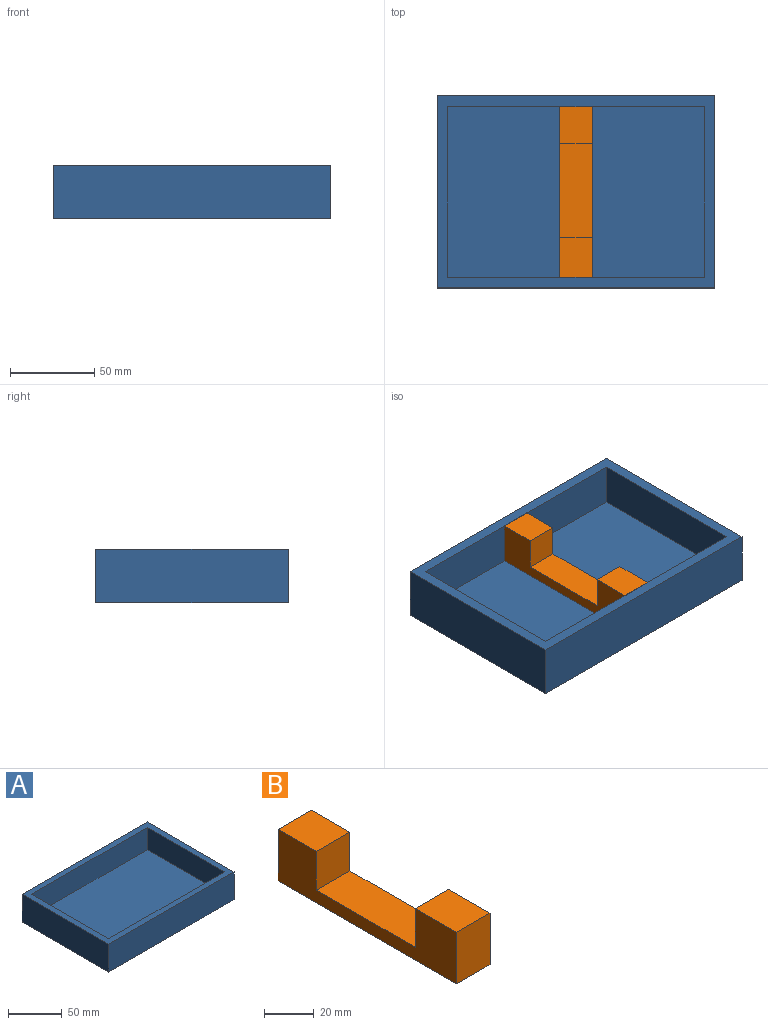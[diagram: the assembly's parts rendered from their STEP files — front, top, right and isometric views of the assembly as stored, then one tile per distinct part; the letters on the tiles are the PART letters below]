
ASSEMBLY  parts=2 mates=1
PART A: 11 faces, bbox 165.1x114.3x31.8 mm
  f0: plane 165.1x114.3mm, normal (0,0,1), area 3387.1mm2, adj f1,f2,f3,f4,f6,f7,f8,f9
  f1: plane 114.3x31.75mm, normal (1,0,0), area 3629mm2, adj f0,f2,f4,f5
  f2: plane 165.1x31.75mm, normal (0,1,0), area 5241.9mm2, adj f0,f1,f3,f5
  f3: plane 114.3x31.75mm, normal (-1,0,0), area 3629mm2, adj f0,f2,f4,f5
  f4: plane 165.1x31.75mm, normal (0,-1,0), area 5241.9mm2, adj f0,f1,f3,f5
  f5: plane 165.1x114.3mm, normal (0,0,-1), area 18870.9mm2, adj f1,f2,f3,f4
  f6: plane 101.6x25.4mm, normal (-1,0,0), area 2580.6mm2, adj f0,f7,f9,f10
  f7: plane 152.4x25.4mm, normal (0,-1,0), area 3871mm2, adj f0,f6,f8,f10
  f8: plane 101.6x25.4mm, normal (1,0,0), area 2580.6mm2, adj f0,f7,f9,f10
  f9: plane 152.4x25.4mm, normal (0,1,0), area 3871mm2, adj f0,f6,f8,f10
  f10: plane 152.4x101.6mm, normal (0,0,1), area 15483.8mm2, adj f6,f7,f8,f9
PART B: 10 faces, bbox 19.1x101.6x25.4 mm
  f0: plane 23.47x19.05mm, normal (0,0,1), area 447.1mm2, adj f1,f5,f6,f7
  f1: plane 101.6x25.4mm, normal (1,0,0), area 1508.4mm2, adj f0,f2,f3,f4,f5,f7,f8,f9
  f2: plane 101.6x19.05mm, normal (0,0,-1), area 1935.5mm2, adj f1,f3,f5,f6
  f3: plane 25.4x19.05mm, normal (0,1,0), area 483.9mm2, adj f1,f2,f4,f6
  f4: plane 21.85x19.05mm, normal (0,0,1), area 416.2mm2, adj f1,f3,f6,f8
  f5: plane 25.4x19.05mm, normal (0,-1,0), area 483.9mm2, adj f0,f1,f2,f6
  f6: plane 101.6x25.4mm, normal (-1,0,0), area 1508.4mm2, adj f0,f2,f3,f4,f5,f7,f8,f9
  f7: plane 19.05x19.05mm, normal (0,1,0), area 362.9mm2, adj f0,f1,f6,f9
  f8: plane 19.05x19.05mm, normal (0,-1,0), area 362.9mm2, adj f1,f4,f6,f9
  f9: plane 56.29x19.05mm, normal (0,0,1), area 1072.2mm2, adj f1,f6,f7,f8
PLACE A t=(-55.53,-72.82,-38.29)mm
PLACE B t=(-65.05,131.46,-82.56)mm
MATE fastened B.f2 <-> A.f10  axis (0,0,-1) through (-55.53,-72.82,-31.94)mm
